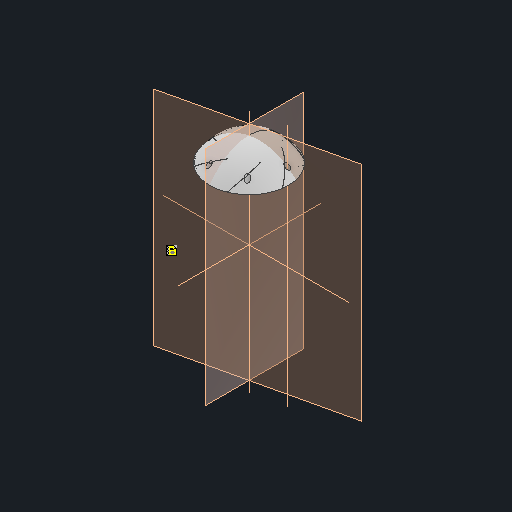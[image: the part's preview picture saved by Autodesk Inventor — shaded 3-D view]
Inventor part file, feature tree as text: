
AUTODESK INVENTOR PART (.ipt)
format: ipt  version: 2023 (Build 270158000, 158)  size: 2,345,984 bytes
history: native  units: mm
features: sketch x23, extrude x14, projected_geometry x12, other x9, reference x8, plane x6, pattern_circular x6, revolve x5, pattern_linear x2, sweep x1, chamfer x1, shell x1
ambient origin geometry x8: Origin, YZ Plane, XZ Plane, XY Plane, X Axis, Y Axis, Z Axis, Center Point
bodies: Solid1 (feature_tree)
feature tree (88):
  revolve  "Revolution1"  [1 undecoded]
  sketch  "3D Sketch1"
  plane  "Work Plane1"
  sweep  "Sweep1"
  pattern_circular  "Circular Pattern1"  Count=6 Angle=360.0deg
  extrude  "Extrusion1"  TaperAngle=0.0deg  [1 undecoded]
  revolve  "Revolution4"  [1 undecoded]
  extrude  "Extrusion10"  Depth=10.0mm
  revolve  "Revolution6"  [1 undecoded]
  pattern_circular  "Circular Pattern8"  Count=3 Angle=360.0deg
  extrude  "Extrusion17"  Depth=6.0mm
  plane  "Work Plane8"
  revolve  "Revolution7"  Angle=45.0deg
  pattern_circular  "Circular Pattern9"  Count=3 Angle=360.0deg
  extrude  "Extrusion12"  Depth=6.0mm
  extrude  "Extrusion13"  Depth=4.0mm TaperAngle=360.0deg
  extrude  "Extrusion14"  Depth=130.0mm
  extrude  "Extrusion15"  TaperAngle=90.0deg  [1 undecoded]
  extrude  "Extrusion16"  Depth=4.0mm
  pattern_linear  "Rectangular Pattern1"  Spacing1=26.0mm  [1 undecoded]
  pattern_linear  "Rectangular Pattern2"  Spacing1=66.5mm  [1 undecoded]
  plane  "Work Plane3"
  sketch  "Sketch12"  dims[d16=0.2mm]
  plane  "Work Plane6"
  extrude  "Extrusion6"  Depth=4.0mm TaperAngle=0.0deg
  chamfer  "Chamfer2"  Distance=25.9mm
  pattern_circular  "Circular Pattern4"  [2 undecoded]
  shell  "Shell2"  Thickness=1.6mm
  extrude  "Extrusion8"  Depth=4.0mm
  extrude  "Extrusion2"  Depth=4.0mm
  sketch  "Sketch7"  dims[d13=1.6mm]
  plane  "Work Plane4"
  extrude  "Extrusion3"  Depth=4.0mm TaperAngle=0.0deg
  extrude  "Extrusion4"  Depth=4.0mm TaperAngle=0.0deg
  pattern_circular  "Circular Pattern2"  [2 undecoded]
  extrude  "Extrusion7"  Depth=10.0mm TaperAngle=0.0deg
  pattern_circular  "Circular Pattern5"  Count=6  [1 undecoded]
  revolve  "Revolution2"  [1 undecoded]
  sketch  "Sketch1"  dims[d0=160.0mm d1=100.0mm]
  other  "Helical Curve2"
  other  "Project to Surface1"
  sketch  "Sketch2"  dims[d2=90.0deg d7=1200.0mm d8=637.649mm d9=252.623mm d10=0.0mm]
  sketch  "Sketch3"  dims[d11=15.0mm]
  plane  "Work Plane2"
  sketch  "Sketch6"  dims[d12=3.0mm]
  sketch  "Sketch8"  dims[d14=1.478932mm]
  sketch  "Sketch9"  dims[d15=0.2mm]
  sketch  "Sketch13"  dims[d17=0.2mm]
  sketch  "Sketch14"  dims[d18=0.0mm d19=0.0mm d20=60.0mm d21=360.0deg]
  reference  "Reference1"
  sketch  "Sketch15"  dims[d23=120.0mm d24=0.0mm d25=0.0mm]
  sketch  "Sketch16"  dims[d26=-130.0mm d27=-10.0mm d29=1.0mm]
  sketch  "Sketch18"  dims[d30=10.0mm d31=0.0mm d32=6.0mm]
  sketch  "Sketch21"  dims[d33=4.0mm d34=0.0mm d35=4.0mm]
  reference  "Reference10"
  sketch  "Sketch24"  dims[d36=4.0mm d37=0.0mm d38=30.0mm d39=360.0deg]
  projected_geometry  "Projected Loop3"
  sketch  "Sketch25"  dims[d51=100.0mm d52=6.0mm]
  projected_geometry  "Projected Loop4"
  sketch  "Sketch26"  dims[d53=4.0mm d54=0.0mm d55=3.5mm d56=1.0mm d57=45.0deg d58=30.0mm d59=360.0deg]
  projected_geometry  "Projected Loop5"
  sketch  "Sketch27"  dims[d61=30.0deg d62=6.0mm]
  sketch  "Sketch28"  dims[d63=4.0mm d64=0.0mm d65=60.0mm d66=360.0deg]
  sketch  "Sketch31"  dims[d68=360.0deg d69=130.0mm]
  sketch  "Sketch32"  dims[d70=0.0mm d71=0.0mm d73=90.0deg]
  reference  "Reference11"
  reference  "Reference12"
  reference  "Reference13"
  reference  "Reference14"
  reference  "Reference15"
  reference  "Reference16"
  other  "Work Axis2"
  sketch  "Sketch33"  dims[d83=5.0mm d84=3.3mm d85=26.0mm d86=0.0mm d89=66.5mm d90=150.0mm d91=0.0mm d92=25.9mm d93=1.6mm d94=0.0mm d95=1.6mm d96=1.6mm d97=1.6mm d98=30.0mm d99=0.0mm d100=30.0mm d101=0.0mm d102=4.0mm d103=10.0mm d104=0.0mm d105=60.0mm d107=10.0mm d108=70.0mm d110=10.0mm d111=100.0mm d113=10.0mm d114=60.0mm d116=10.0mm d117=1.3mm d118=1.3mm d124=1.2mm d125=6.457718mm d126=60.0mm d127=360.0deg d129=0.0mm d130=0.0mm d131=5.0mm d132=4.0mm d133=90.0deg d134=60.0mm d135=360.0deg]
  projected_geometry  "Projected Loop7"
  projected_geometry  "Project Cut Edges1"
  projected_geometry  "Project Cut Edges2"
  projected_geometry  "Project Cut Edges3"
  projected_geometry  "Project Cut Edges5"
  projected_geometry  "Project Cut Edges6"
  parser-record x2  (decoder bookkeeping rows leaked as tree rows — omitted from the tree; the rows remain in map.json)
  other  "Assembly1.iam"
  other  "lower_centering_ring:1"
  projected_geometry  "Project Cut Edges7"
  projected_geometry  "Project Cut Edges9"
  other  "assembly.iam"
  other  "ring_oben:1"
  projected_geometry  "Project Cut Edges10"
note: 13 required parameter values undecoded (feature->parameter linkage not recoverable at this tier; creation-order binding heuristic only, values carry confidence <= 0.55)
note: 2 file-system paths scrubbed to <path> (originals preserved in map.json)